# Revit family: QF_ELECTROLUXPROFESSIONAL_391399_E9IINIAOMEA
name_source: partatom
category: Specialty Equipment
revit_build: Autodesk Revit 2018 (Build: 20190510_1515(x64)
units: mm (PartAtom-declared; Revit-internal decimal feet)

## family parameters
Always vertical = Yes
Cut with Voids When Loaded = No
Part Type = Normal
Room Calculation Point = No
Round Connector Dimension = Use Diameter
Shared = No
Work Plane-Based = No

## types (1)
- QF_ELECTROLUXPROFESSIONAL_391399_E9IINIAOMEA
    50 Hertz Option = Yes
    60 Hertz Option = No
    Apparent Power = 15000 VA
    Conn Conduit = Yes
    Cycle = 50 Hz
    Depth = 930 mm  [stored 3.05118 ft]
    Description = 900XP FULL MODULE ELECTRIC FRY TOP,SMOOTH HORIZONTAL PLATE, MILD STEEL -230 V
    Direct Waste Size = 0"
    FL Amps = 38 A
    HP = 20.1 HP
    Height = 410 mm  [stored 1.34514 ft]
    Manufacturer = ELECTROLUX
    Max Overcurrent Protection = 0 A
    Min Ckt Ampacity = 0 A
    Model = 391173
    Phase = 3
    URL = www.electrolux.com
    URL Cutsheet = www.electrolux.com
    Volts = 230 V
    Watts = 15000 W
    Weight in Pounds = 105
    Width = 800 mm  [stored 2.62467 ft]

note: [stored X ft] marks values corroborated as IEEE doubles in the binary element streams (Revit-internal decimal feet)

## geometry (parser evidence)
native form markers: Blend x8, Sweep x2
no freeform markers — native parametric forms only
